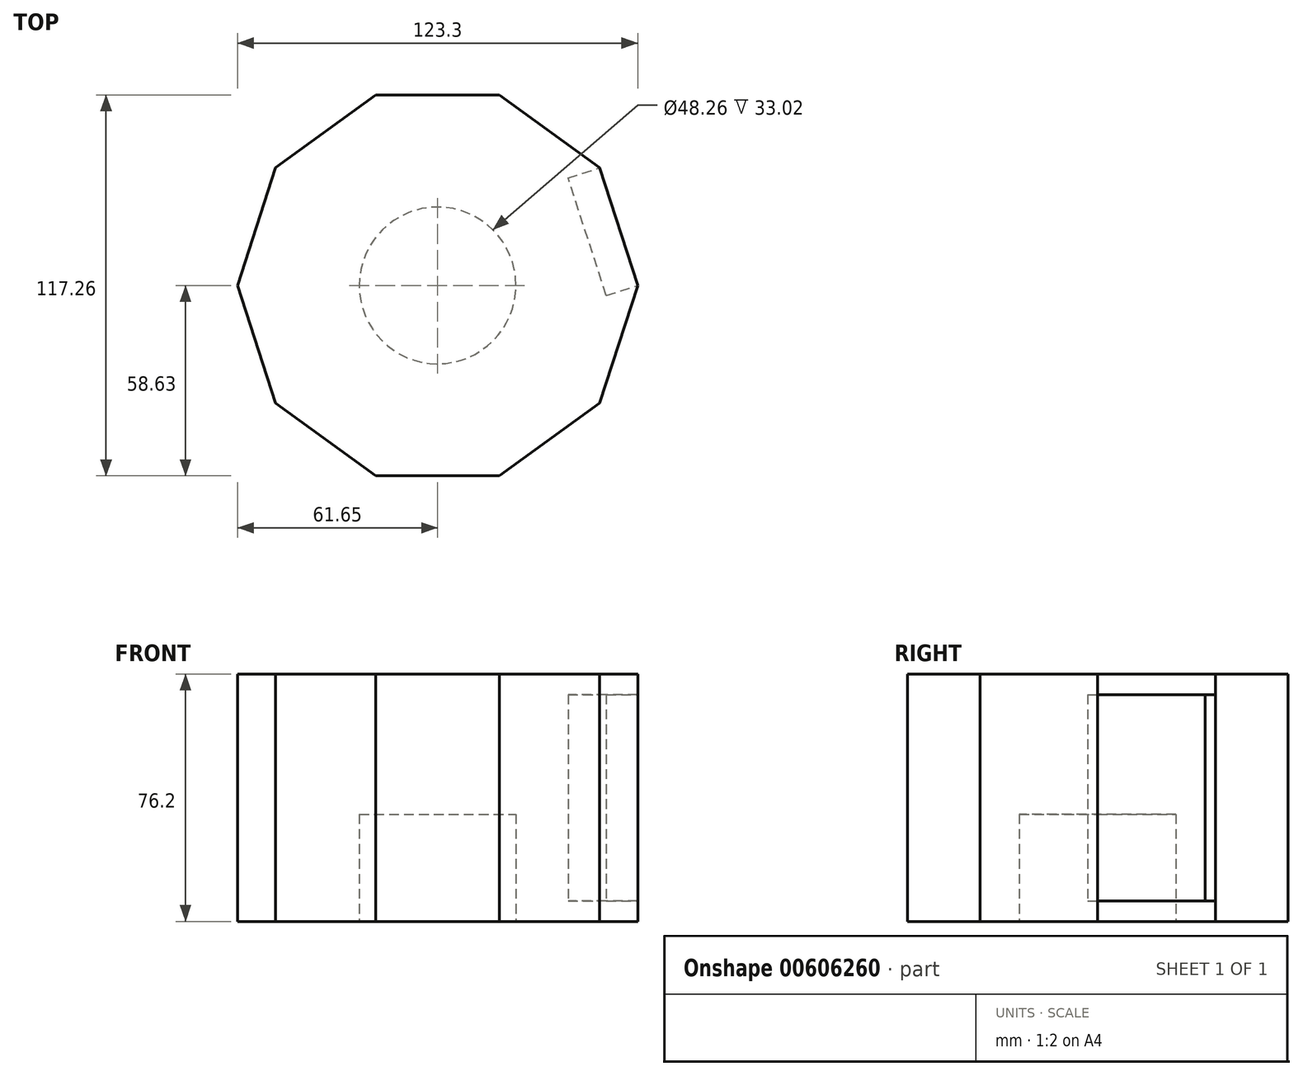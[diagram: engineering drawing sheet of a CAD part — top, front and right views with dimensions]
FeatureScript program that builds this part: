
annotation { "Feature Type Name" : "Feature", "Feature Type Description" : "" }
export const myFeature = defineFeature(function(context is Context, id is Id, definition is map)
    precondition{}
    {
        {
            var Q0;
            Q0=qCreatedBy(makeId("Top.planeOp"),FACE);
            var sketch = newSketch(context, id + "F0", { "sketchPlane" : qUnion([Q0])});
            skCircle(sketch, "E0.cCircle", {"center": v(0, 0) * mm, "radius": 58.63 * mm, "construction": true});
            skLineSegment(sketch, "E0.0", {"start": v(-19.05, 58.63) * mm, "end": v(19.05, 58.63) * mm});
            skLineSegment(sketch, "E0.1", {"start": v(19.05, 58.63) * mm, "end": v(49.87, 36.24) * mm});
            skLineSegment(sketch, "E0.2", {"start": v(49.87, 36.24) * mm, "end": v(61.65, 0) * mm});
            skLineSegment(sketch, "E0.3", {"start": v(61.65, 0) * mm, "end": v(49.87, -36.24) * mm});
            skLineSegment(sketch, "E0.4", {"start": v(49.87, -36.24) * mm, "end": v(19.05, -58.63) * mm});
            skLineSegment(sketch, "E0.5", {"start": v(19.05, -58.63) * mm, "end": v(-19.05, -58.63) * mm});
            skLineSegment(sketch, "E0.6", {"start": v(-19.05, -58.63) * mm, "end": v(-49.87, -36.24) * mm});
            skLineSegment(sketch, "E0.7", {"start": v(-49.87, -36.24) * mm, "end": v(-61.65, 0) * mm});
            skLineSegment(sketch, "E0.8", {"start": v(-61.65, 0) * mm, "end": v(-49.87, 36.24) * mm});
            skLineSegment(sketch, "E0.9", {"start": v(-49.87, 36.24) * mm, "end": v(-19.05, 58.63) * mm});
            skPoint(sketch, "E0.0.midPoint", {"position": v(0, 58.63) * mm});
            skSolve(sketch);
        }
        {
            var Q0;
            Q0 = qSketchRegion(id + "F0", true);
            extrude(context, id + "F1", {"entities" : qUnion([Q0]), "depth" : 76.2 * mm, "offsetDistance" : 25.4 * mm});
        }
        {
            var Q0;
            Q0=makeQuery(id+"F1.opExtrude","CAP_FACE",FACE,{"disambiguationData":[OSD([sQuery(id+"F0.wireOp",EDGE,"E0.0"),sQuery(id+"F0.wireOp",EDGE,"E0.1"),sQuery(id+"F0.wireOp",EDGE,"E0.2"),sQuery(id+"F0.wireOp",EDGE,"E0.3"),sQuery(id+"F0.wireOp",EDGE,"E0.4"),sQuery(id+"F0.wireOp",EDGE,"E0.5"),sQuery(id+"F0.wireOp",EDGE,"E0.6"),sQuery(id+"F0.wireOp",EDGE,"E0.7"),sQuery(id+"F0.wireOp",EDGE,"E0.8"),sQuery(id+"F0.wireOp",EDGE,"E0.9")])],"isStart":true});
            var sketch = newSketch(context, id + "F2", { "sketchPlane" : qUnion([Q0])});
            skCircle(sketch, "E1", {"center": v(0, 0) * mm, "radius": 24.13 * mm});
            skSolve(sketch);
        }
        {
            var Q0;
            Q0 = qSketchRegion(id + "F2", true);
            extrude(context, id + "F3", {"entities" : qUnion([Q0]), "operationType" : NewBodyOperationType.REMOVE, "oppositeDirection" : true, "depth" : 33.02 * mm, "offsetDistance" : 25.4 * mm});
        }
        {
            var Q0;
            Q0=makeQuery(id+"F1.opExtrude","SWEPT_FACE",FACE,{"disambiguationData":[OSD([sQuery(id+"F0.wireOp",EDGE,"E0.2")])]});
            var sketch = newSketch(context, id + "F4", { "sketchPlane" : qUnion([Q0])});
            skLineSegment(sketch, "E2.bottom", {"start": v(-19.05, 69.85) * mm, "end": v(19.05, 69.85) * mm});
            skLineSegment(sketch, "E2.top", {"start": v(-19.05, 6.35) * mm, "end": v(19.05, 6.35) * mm});
            skLineSegment(sketch, "E2.left", {"start": v(-19.05, 69.85) * mm, "end": v(-19.05, 6.35) * mm});
            skLineSegment(sketch, "E2.right", {"start": v(19.05, 69.85) * mm, "end": v(19.05, 6.35) * mm});
            skSolve(sketch);
        }
        {
            var Q0;
            Q0 = qSketchRegion(id + "F4", true);
            extrude(context, id + "F5", {"entities" : qUnion([Q0]), "operationType" : NewBodyOperationType.REMOVE, "oppositeDirection" : true, "depth" : 10.16 * mm, "offsetDistance" : 25.4 * mm});
        }
    });
